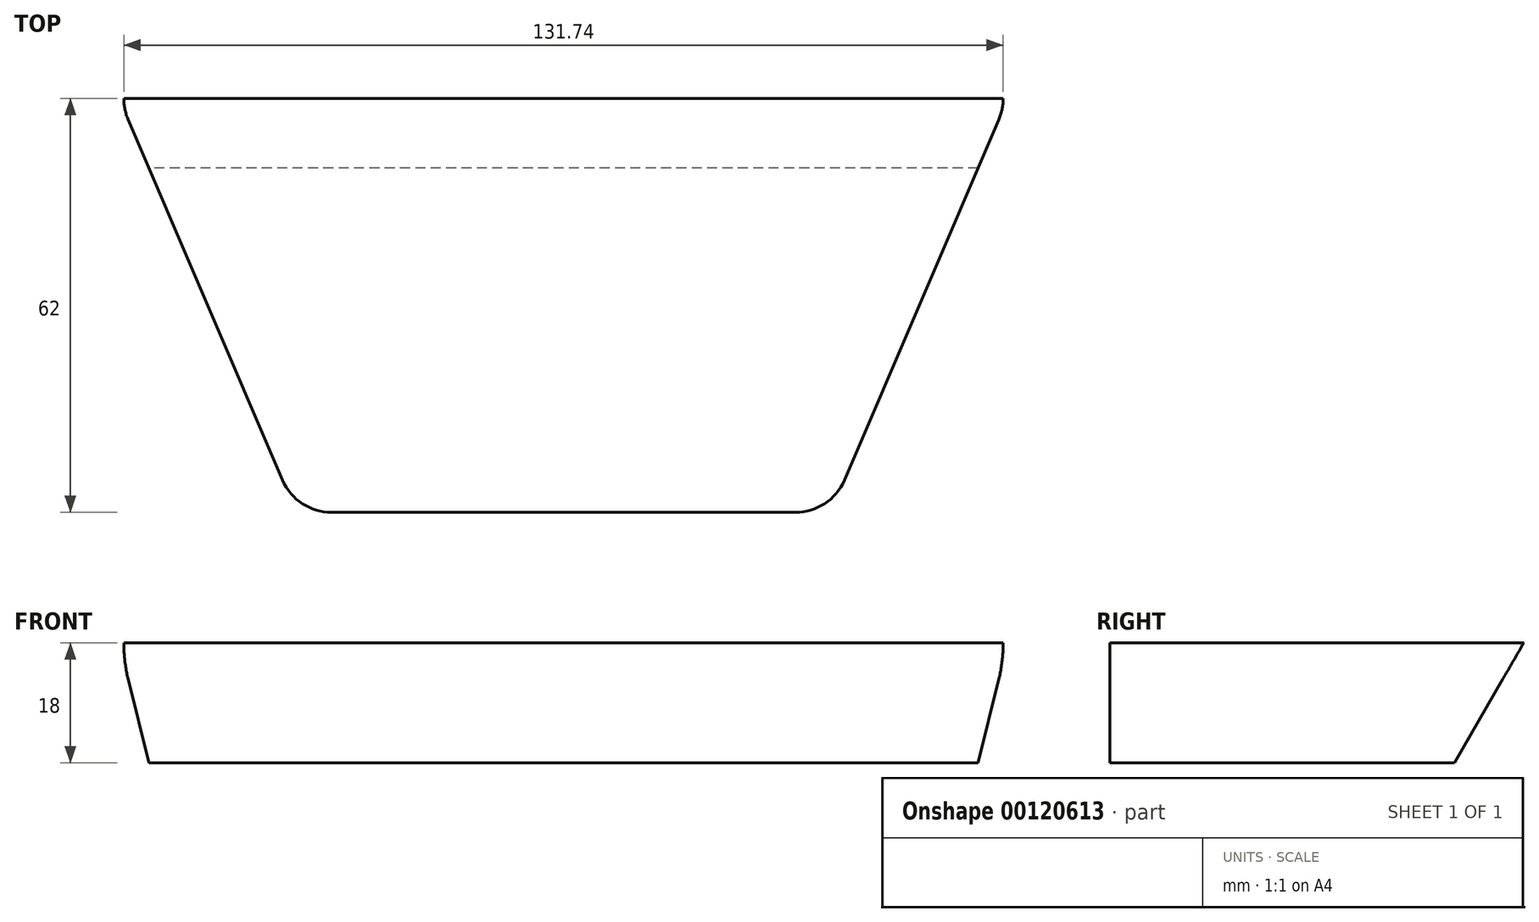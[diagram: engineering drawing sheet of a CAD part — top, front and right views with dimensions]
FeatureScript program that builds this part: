
annotation { "Feature Type Name" : "Feature", "Feature Type Description" : "" }
export const myFeature = defineFeature(function(context is Context, id is Id, definition is map)
    precondition{}
    {
        {
            var Q0;
            Q0=qCreatedBy(makeId("Top.planeOp"),FACE);
            var sketch = newSketch(context, id + "F0", { "sketchPlane" : qUnion([Q0])});
            skLineSegment(sketch, "E0", {"start": v(-57.87, 35) * mm, "end": v(57.87, 35) * mm});
            skPoint(sketch, "E1", {"position": v(0, 35) * mm});
            skLineSegment(sketch, "E2", {"start": v(-34.72, -35) * mm, "end": v(34.72, -35) * mm});
            skPoint(sketch, "E3", {"position": v(0, -35) * mm});
            skLineSegment(sketch, "E4", {"start": v(65.22, 23.85) * mm, "end": v(42.08, -30.15) * mm});
            skLineSegment(sketch, "E5", {"start": v(-65.22, 23.85) * mm, "end": v(-42.08, -30.15) * mm});
            skPoint(sketch, "E6.visualSharp", {"position": v(-70, 35) * mm});
            skArc(sketch, "E6.filletArc", {"start": v(-57.87, 35) * mm, "mid": v(-64.55, 31.4) * mm, "end": v(-65.22, 23.85) * mm});
            skPoint(sketch, "E7.visualSharp", {"position": v(70, 35) * mm});
            skArc(sketch, "E7.filletArc", {"start": v(65.22, 23.85) * mm, "mid": v(64.55, 31.4) * mm, "end": v(57.87, 35) * mm});
            skPoint(sketch, "E8.visualSharp", {"position": v(-40, -35) * mm});
            skArc(sketch, "E8.filletArc", {"start": v(-42.08, -30.15) * mm, "mid": v(-39.13, -33.68) * mm, "end": v(-34.72, -35) * mm});
            skPoint(sketch, "E9.visualSharp", {"position": v(40, -35) * mm});
            skArc(sketch, "E9.filletArc", {"start": v(34.72, -35) * mm, "mid": v(39.13, -33.68) * mm, "end": v(42.08, -30.15) * mm});
            skSolve(sketch);
        }
        {
            var Q0;
            Q0 = qSketchRegion(id + "F0", true);
            extrude(context, id + "F1", {"entities" : qUnion([Q0]), "depth" : 18 * mm});
        }
        {
            var Q0;
            Q0=qCreatedBy(makeId("Right.planeOp"),FACE);
            var sketch = newSketch(context, id + "F2", { "sketchPlane" : qUnion([Q0])});
            skLineSegment(sketch, "E10", {"start": v(0, 0) * mm, "end": v(27, 0) * mm});
            skLineSegment(sketch, "E11", {"start": v(27, 0) * mm, "end": v(27, 18) * mm});
            skLineSegment(sketch, "E12", {"start": v(27, 18) * mm, "end": v(16.6, 0) * mm});
            skLineSegment(sketch, "E13.bottom", {"start": v(27, 18) * mm, "end": v(35, 18) * mm});
            skLineSegment(sketch, "E13.top", {"start": v(27, 0) * mm, "end": v(35, 0) * mm});
            skLineSegment(sketch, "E13.left", {"start": v(27, 18) * mm, "end": v(27, 0) * mm});
            skLineSegment(sketch, "E13.right", {"start": v(35, 18) * mm, "end": v(35, 0) * mm});
            skSolve(sketch);
        }
        {
            var Q0;
            {var subQ2=sQuery(id+"F2.wireOp",EDGE,"E12");Q0=makeQuery(id+"F2.imprint","IMPRINT",FACE,{"disambiguationData":[TD([[makeQuery(id+"F2.imprint","IMPRINT",EDGE,{"derivedFrom":subQ2}),1.0]])]});}
            var Q1;
            Q1=makeQuery(id+"F2.imprint","IMPRINT",FACE,{"disambiguationData":[TD([[makeQuery(id+"F2.imprint","IMPRINT",EDGE,{"derivedFrom":sQuery(id+"F2.wireOp",EDGE,"E13.bottom")}),-1.0]])]});
            extrude(context, id + "F3", {"entities" : qUnion([Q0, Q1]), "operationType" : NewBodyOperationType.REMOVE, "endBound" : BoundingType.SYMMETRIC, "depth" : 140 * mm});
        }
    });
